# Revit family: Building-IEC309Boards-GEWISS-68QDIN-DISTRIBUTION-BOARD-20MOD_6SOCKET-OUTLETS
name_source: partatom
category: Attrezzatura elettrica
revit_build: Autodesk Revit 2016 (Build: 20161004_0715(x64)
units: mm (PartAtom-declared; Revit-internal decimal feet)

## family parameters
Condiviso = No
Configurazione quadro = Due colonne, circuiti in orizzontale
Host = Muro
Numero OmniClass = 23.80.30.11.17
Punto di calcolo locali = No
Quota connettore circolare = Usa diametro
Sempre verticale = Sì
Taglio con vuoti quando caricato = No
Tipo di parte = Pannello comandi
Titolo OmniClass = Distribution Boards and Control Panels

## types (1)
- GW68021N - Q-DIN 20M 2S.O.63A 4S.O.16/32A IP65
    Accordance with Standards = EN 60208 - EN 60670-1 - IEC 60670-24
    Altezza = 560 mm  [stored 1.83727 ft]
    Carico apparente = 0 VA
    Catalogue = BUILDING
    Catalogue Range = 68 QDIN
    Classificazione carico = Altro
    Colour = Grey RAL 7035
    Descrizione = Q-DIN 20M 2S.O.63A 4S.O.16/32A IP65
    Dispersible power A (W) = 30
    Dispersible power B (W) = 92
    EAN code = 8011564744882
    Electrocod = 2242
    Glow Wire Test = 650°C
    H_da terra = 1200 mm  [stored 3.93701 ft]
    Houseable socket = 2 IEC 309 63A - 4 IEC 309 16/32A
    IDF = 7fc76941-0cea-4757-b7ec-a7896b62d45f
    IDT = c4e5c53f-a295-41ab-9992-af314b14205a
    IP degree = IP65
    Immagine tipo = GW68021N.jpg
    Installation type = Surface-mounting
    Insulation class = II
    Lunghezza = 450 mm  [stored 1.47638 ft]
    Modello = GW68021N
    No. of modules EN 50022 = 20
    No. of provided blank lids = 2 IEC 309 16/32A+1 63A
    Numero di poli = 3
    Operating temperature: = -25 +40 °C
    Presa = GEWISS - Grigio RAL - 7035
    Produttore = GEWISS S.p.A.
    SEO = Board
    Shock resistance = IK08
    Struttura = GEWISS - Grigio RAL - 7035
    Technical sheet = https://www.gewiss.com
    Thermo-pressure with ball = 70
    URL = https://www.gewiss.com
    Version file RFA = 18.0
    Version type = Empty
    Vetro = GEWISS - vetro
    Voltaggio = 400V
    potenza = 400 V

note: source unit labels omitted for Thermo-pressure with ball — the stored unit's dimension contradicts the parameter name (converter mislabeling)

note: [stored X ft] marks values corroborated as IEEE doubles in the binary element streams (Revit-internal decimal feet)

## geometry (parser evidence)
native form markers: Sweep x3
no freeform markers — native parametric forms only
